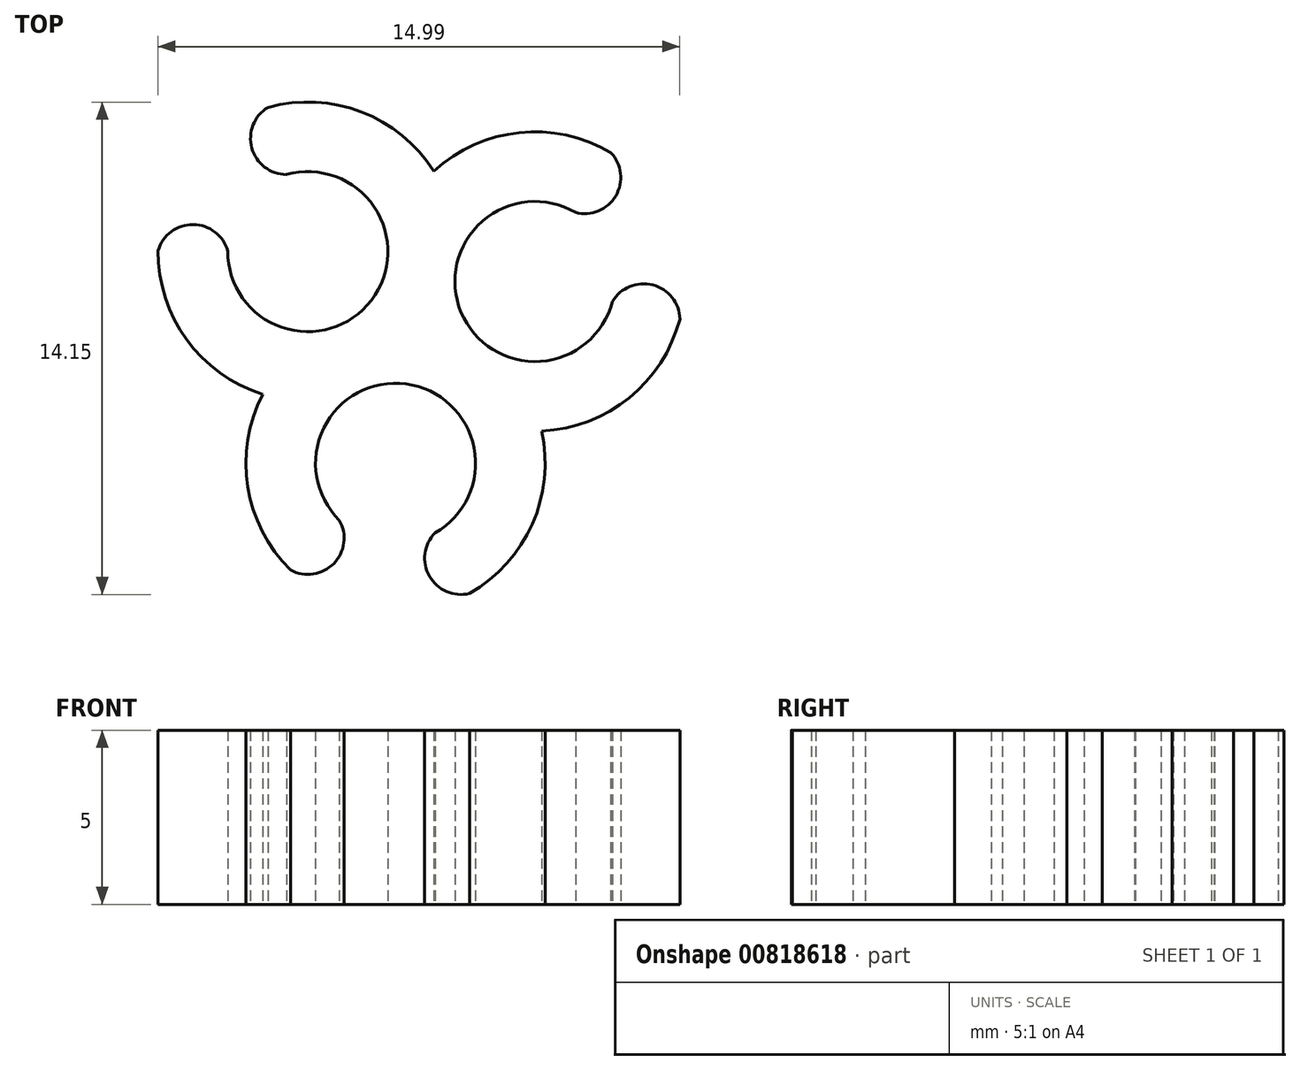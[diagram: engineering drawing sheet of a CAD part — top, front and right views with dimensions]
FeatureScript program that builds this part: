
annotation { "Feature Type Name" : "Feature", "Feature Type Description" : "" }
export const myFeature = defineFeature(function(context is Context, id is Id, definition is map)
    precondition{}
    {
        {
            var Q0;
            Q0=qCreatedBy(makeId("Top.planeOp"),FACE);
            var sketch = newSketch(context, id + "F0", { "sketchPlane" : qUnion([Q0])});
            skArc(sketch, "E0", {"start": v(-5.32, 2.33) * mm, "mid": v(-1.2, 0.91) * mm, "end": v(-3.63, 4.53) * mm});
            skArc(sketch, "E1", {"start": v(-7.32, 2.34) * mm, "mid": v(-6.5, -0.22) * mm, "end": v(-4.31, -1.79) * mm});
            skLineSegment(sketch, "E2", {"start": v(-0.26, 0.4) * mm, "end": v(-0.35, 0.53) * mm});
            skArc(sketch, "E3", {"start": v(-4.16, 6.46) * mm, "mid": v(-4.62, 5.3) * mm, "end": v(-3.63, 4.53) * mm});
            skArc(sketch, "E4.MirrorCS", {"start": v(-7.32, 2.34) * mm, "mid": v(-6.3, 3.1) * mm, "end": v(-5.32, 2.33) * mm});
            skArc(sketch, "E5.1.1", {"start": v(1.63, -7.5) * mm, "mid": v(0.48, -7.01) * mm, "end": v(0.64, -5.77) * mm});
            skArc(sketch, "E5.1.2", {"start": v(1.63, -7.5) * mm, "mid": v(3.43, -5.52) * mm, "end": v(3.7, -2.84) * mm});
            skArc(sketch, "E5.1.3", {"start": v(0.64, -5.77) * mm, "mid": v(-0.2, -1.49) * mm, "end": v(-2.1, -5.4) * mm});
            skArc(sketch, "E5.1.4", {"start": v(-3.51, -6.83) * mm, "mid": v(-2.27, -6.65) * mm, "end": v(-2.1, -5.4) * mm});
            skArc(sketch, "E5.2.1", {"start": v(5.69, 5.16) * mm, "mid": v(5.83, 3.92) * mm, "end": v(4.67, 3.44) * mm});
            skArc(sketch, "E5.2.2", {"start": v(5.69, 5.16) * mm, "mid": v(3.06, 5.73) * mm, "end": v(0.6, 4.63) * mm});
            skArc(sketch, "E5.2.3", {"start": v(4.67, 3.44) * mm, "mid": v(1.39, 0.57) * mm, "end": v(5.74, 0.88) * mm});
            skArc(sketch, "E5.2.4", {"start": v(7.67, 0.38) * mm, "mid": v(6.9, 1.36) * mm, "end": v(5.74, 0.88) * mm});
            skPoint(sketch, "E5.center", {"position": v(0, 0) * mm});
            skArc(sketch, "E6.trimOffspring", {"start": v(0, 3.8) * mm, "mid": v(-0.05, 3.8) * mm, "end": v(-0.1, 3.8) * mm});
            skArc(sketch, "E7.trimOffspring", {"start": v(0.71, -1.8) * mm, "mid": v(0.9, -1.96) * mm, "end": v(1.08, -2.1) * mm});
            skArc(sketch, "E8.trimOffspring", {"start": v(-0.35, 0.27) * mm, "mid": v(-0.3, 0.33) * mm, "end": v(-0.26, 0.4) * mm});
            skArc(sketch, "E9.trimOffspring", {"start": v(-1.92, 0.29) * mm, "mid": v(-2.14, 0.2) * mm, "end": v(-2.35, 0.1) * mm});
            skArc(sketch, "E10.trimOffspring", {"start": v(0.24, -0.5) * mm, "mid": v(0.4, -0.3) * mm, "end": v(0.54, -0.1) * mm});
            skArc(sketch, "E11.trimOffspring", {"start": v(3.7, -2.84) * mm, "mid": v(6.22, -1.89) * mm, "end": v(7.67, 0.38) * mm});
            skArc(sketch, "E12.trimOffspring", {"start": v(2.3, -0.5) * mm, "mid": v(2.12, -0.36) * mm, "end": v(1.93, -0.22) * mm});
            skArc(sketch, "E13.trimOffspring", {"start": v(1.21, 1.52) * mm, "mid": v(1.25, 1.75) * mm, "end": v(1.27, 1.98) * mm});
            skArc(sketch, "E14.trimOffspring", {"start": v(0.3, 0.46) * mm, "mid": v(0.4, 0.17) * mm, "end": v(0.54, -0.1) * mm});
            skArc(sketch, "E15.trimOffspring", {"start": v(-1.59, -1.74) * mm, "mid": v(-1.37, -1.66) * mm, "end": v(-1.16, -1.56) * mm});
            skArc(sketch, "E16.trimOffspring", {"start": v(-0.72, 2.25) * mm, "mid": v(-0.75, 2.02) * mm, "end": v(-0.78, 1.78) * mm});
            skArc(sketch, "E17.trimOffspring", {"start": v(0.6, 4.63) * mm, "mid": v(-1.48, 6.33) * mm, "end": v(-4.16, 6.46) * mm});
            skArc(sketch, "E18.trimOffspring", {"start": v(-0.69, 0.53) * mm, "mid": v(-0.63, 0.28) * mm, "end": v(-0.55, 0.04) * mm});
            skArc(sketch, "E19.trimOffspring", {"start": v(-4.31, -1.79) * mm, "mid": v(-4.74, -4.44) * mm, "end": v(-3.51, -6.83) * mm});
            skSolve(sketch);
        }
        {
            var Q0;
            Q0=makeQuery(id+"F0.imprint","IMPRINT",FACE,{"disambiguationData":[TD([[makeQuery(id+"F0.imprint","IMPRINT",EDGE,{"derivedFrom":sQuery(id+"F0.wireOp",EDGE,"E1")}),1.0]])]});
            extrude(context, id + "F1", {"entities" : qUnion([Q0]), "depth" : 5 * mm, "offsetDistance" : 25 * mm});
        }
    });
